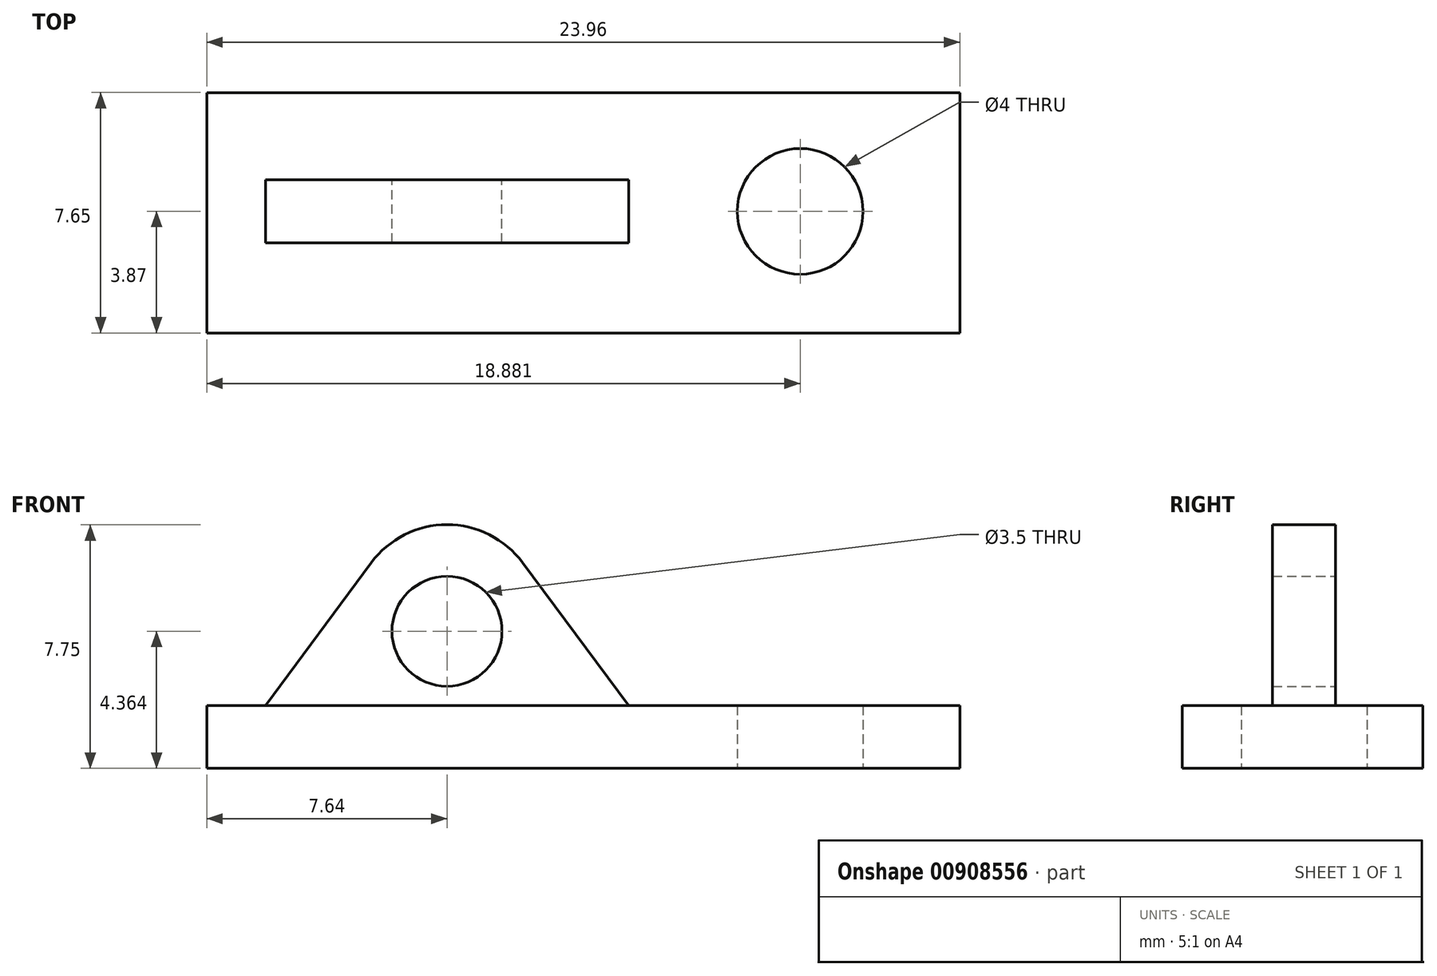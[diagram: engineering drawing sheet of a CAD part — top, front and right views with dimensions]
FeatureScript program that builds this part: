
annotation { "Feature Type Name" : "Feature", "Feature Type Description" : "" }
export const myFeature = defineFeature(function(context is Context, id is Id, definition is map)
    precondition{}
    {
        {
            var Q0;
            Q0=qCreatedBy(makeId("Top.planeOp"),FACE);
            var sketch = newSketch(context, id + "F0", { "sketchPlane" : qUnion([Q0])});
            skLineSegment(sketch, "E0.bottom", {"start": v(-7.64, -3.87) * mm, "end": v(16.32, -3.87) * mm});
            skLineSegment(sketch, "E0.top", {"start": v(-7.64, 3.78) * mm, "end": v(16.32, 3.78) * mm});
            skLineSegment(sketch, "E0.left", {"start": v(-7.64, -3.87) * mm, "end": v(-7.64, 3.78) * mm});
            skLineSegment(sketch, "E0.right", {"start": v(16.32, -3.87) * mm, "end": v(16.32, 3.78) * mm});
            skCircle(sketch, "E1", {"center": v(11.24, 0) * mm, "radius": 2 * mm});
            skSolve(sketch);
        }
        {
            var Q0;
            Q0=makeQuery(id+"F0.imprint","IMPRINT",FACE,{"disambiguationData":[TD([[makeQuery(id+"F0.imprint","IMPRINT",EDGE,{"derivedFrom":sQuery(id+"F0.wireOp",EDGE,"GGk2sLDj-M6VI-7U0P-lLIJ-D1OAGZNEwoZo")}),1.0]])]});
            var Q1;
            Q1=makeQuery(id+"F0.imprint","IMPRINT",FACE,{"disambiguationData":[TD([[makeQuery(id+"F0.imprint","IMPRINT",EDGE,{"derivedFrom":sQuery(id+"F0.wireOp",EDGE,"E0.bottom")}),1.0]])]});
            var Q2;
            Q2=sQuery(id+"F0.wireOp",EDGE,"GGk2sLDj-M6VI-7U0P-lLIJ-D1OAGZNEwoZo");
            extrude(context, id + "F1", {"entities" : qUnion([Q0, Q1]), "surfaceEntities" : qUnion([Q2]), "depth" : 2 * mm, "offsetDistance" : 25 * mm});
        }
        {
            var Q0;
            Q0=qCreatedBy(makeId("Front.planeOp"),FACE);
            var sketch = newSketch(context, id + "F2", { "sketchPlane" : qUnion([Q0])});
            skLineSegment(sketch, "E2", {"start": v(-5.78, 2) * mm, "end": v(-2.4, 6.54) * mm});
            skLineSegment(sketch, "E3", {"start": v(2.4, 6.54) * mm, "end": v(5.78, 2) * mm});
            skLineSegment(sketch, "E4", {"start": v(5.78, 2) * mm, "end": v(-5.78, 2) * mm});
            skPoint(sketch, "E5.visualSharp", {"position": v(0, 9.79) * mm});
            skArc(sketch, "E5.filletArc", {"start": v(2.4, 6.54) * mm, "mid": v(0, 7.75) * mm, "end": v(-2.4, 6.54) * mm});
            skCircle(sketch, "E6", {"center": v(0, 4.36) * mm, "radius": 1.75 * mm});
            skSolve(sketch);
        }
        {
            var Q0;
            Q0=makeQuery(id+"F2.imprint","IMPRINT",FACE,{"disambiguationData":[TD([[makeQuery(id+"F2.imprint","IMPRINT",EDGE,{"derivedFrom":sQuery(id+"F2.wireOp",EDGE,"E2")}),-1.0]])]});
            extrude(context, id + "F3", {"entities" : qUnion([Q0]), "operationType" : NewBodyOperationType.ADD, "endBound" : BoundingType.SYMMETRIC, "depth" : 2 * mm, "offsetDistance" : 25 * mm});
        }
    });
